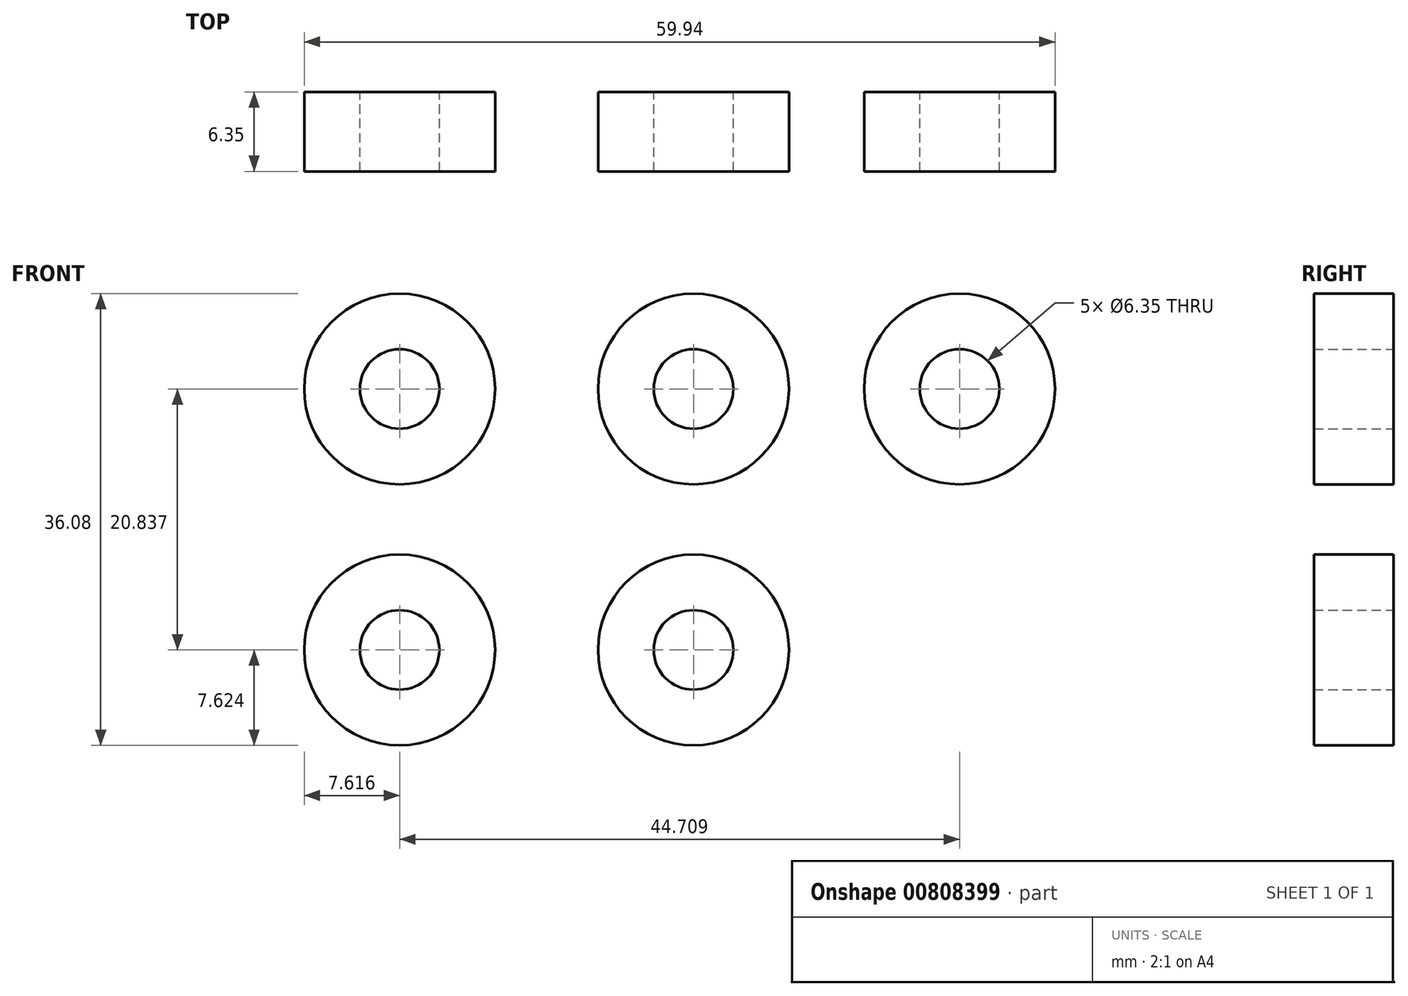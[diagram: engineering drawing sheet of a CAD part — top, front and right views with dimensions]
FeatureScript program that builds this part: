
annotation { "Feature Type Name" : "Feature", "Feature Type Description" : "" }
export const myFeature = defineFeature(function(context is Context, id is Id, definition is map)
    precondition{}
    {
        {
            var Q0;
            Q0=qCreatedBy(makeId("Front.planeOp"),FACE);
            var sketch = newSketch(context, id + "F0", { "sketchPlane" : qUnion([Q0])});
            skCircle(sketch, "E0", {"center": v(-54.82, 37.02) * mm, "radius": 3.18 * mm});
            skCircle(sketch, "E1", {"center": v(-54.82, 37.02) * mm, "radius": 7.62 * mm});
            skCircle(sketch, "E2", {"center": v(-31.36, 37.02) * mm, "radius": 3.18 * mm});
            skCircle(sketch, "E3", {"center": v(-31.36, 37.02) * mm, "radius": 7.62 * mm});
            skCircle(sketch, "E4", {"center": v(-10.12, 37.02) * mm, "radius": 3.18 * mm});
            skCircle(sketch, "E5", {"center": v(-10.12, 37.02) * mm, "radius": 7.62 * mm});
            skCircle(sketch, "E6", {"center": v(-54.82, 16.18) * mm, "radius": 3.18 * mm});
            skCircle(sketch, "E7", {"center": v(-54.82, 16.18) * mm, "radius": 7.62 * mm});
            skCircle(sketch, "E8", {"center": v(-31.36, 16.18) * mm, "radius": 3.18 * mm});
            skCircle(sketch, "E9", {"center": v(-31.36, 16.18) * mm, "radius": 7.62 * mm});
            skSolve(sketch);
        }
        {
            var Q0;
            Q0 = qSketchRegion(id + "F0", true);
            extrude(context, id + "F1", {"entities" : qUnion([Q0]), "depth" : 6.35 * mm, "offsetDistance" : 25.4 * mm});
        }
    });
